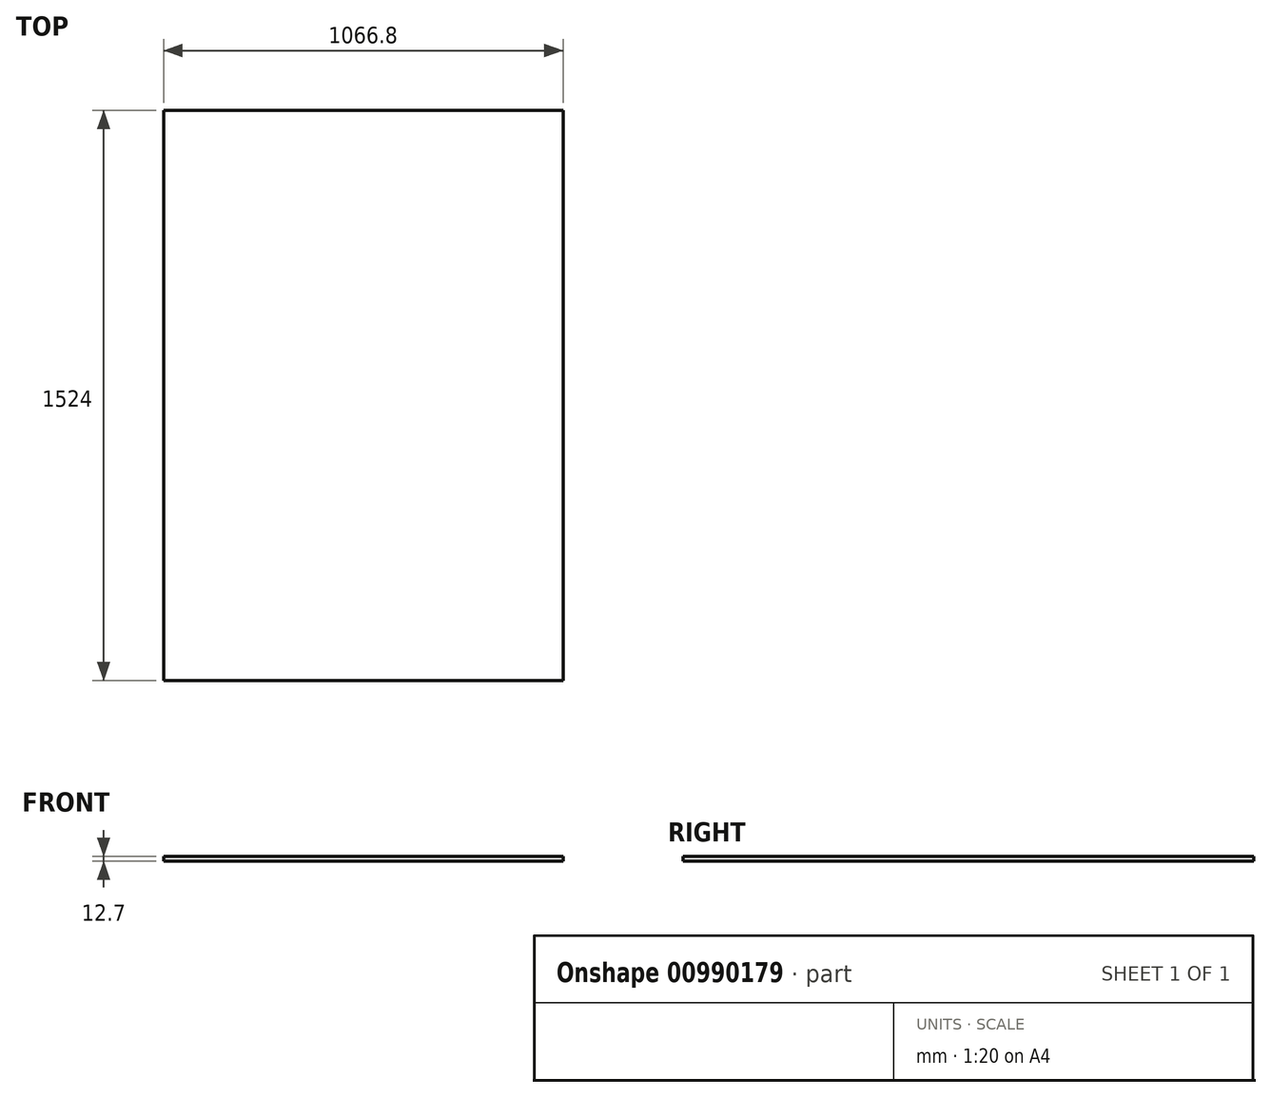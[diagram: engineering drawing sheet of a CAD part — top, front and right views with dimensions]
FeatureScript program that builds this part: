
annotation { "Feature Type Name" : "Feature", "Feature Type Description" : "" }
export const myFeature = defineFeature(function(context is Context, id is Id, definition is map)
    precondition{}
    {
        {
            var Q0;
            Q0=qCreatedBy(makeId("Top.planeOp"),FACE);
            var sketch = newSketch(context, id + "F0", { "sketchPlane" : qUnion([Q0])});
            skLineSegment(sketch, "E0.bottom", {"start": v(533.4, 762) * mm, "end": v(-533.4, 762) * mm});
            skLineSegment(sketch, "E0.top", {"start": v(533.4, -762) * mm, "end": v(-533.4, -762) * mm});
            skLineSegment(sketch, "E0.left", {"start": v(533.4, 762) * mm, "end": v(533.4, -762) * mm});
            skLineSegment(sketch, "E0.right", {"start": v(-533.4, 762) * mm, "end": v(-533.4, -762) * mm});
            skPoint(sketch, "E0.middle", {"position": v(0, 0) * mm});
            skSolve(sketch);
        }
        {
            var Q0;
            Q0=qSketchRegion(id+"F0",true);
            extrude(context, id + "F1", {"entities" : qUnion([Q0]), "depth" : 12.7 * mm, "offsetDistance" : 25.4 * mm});
        }
    });
